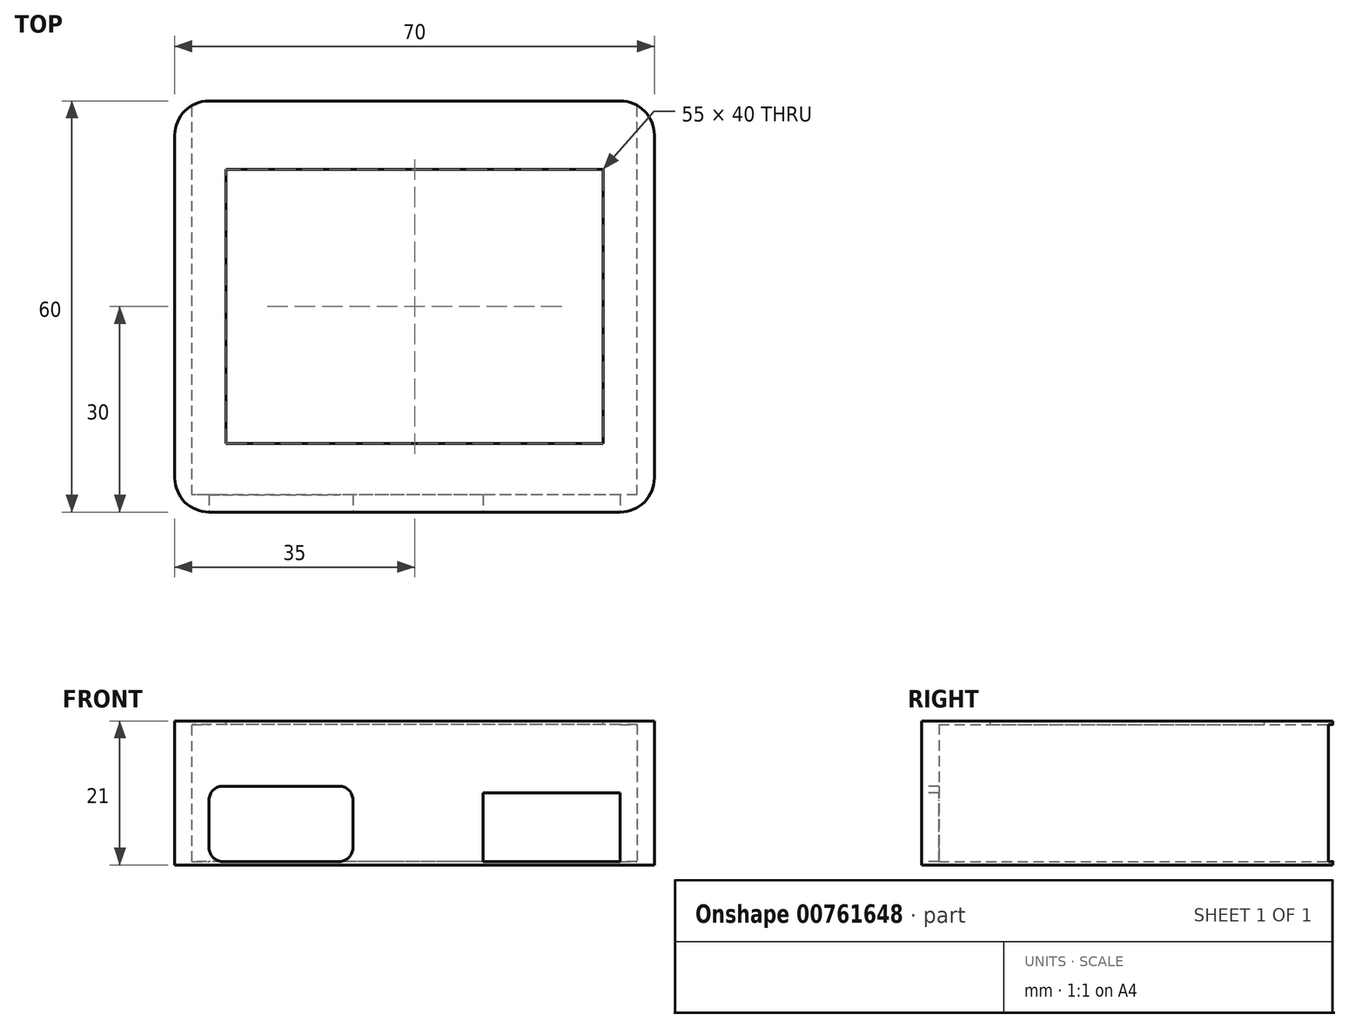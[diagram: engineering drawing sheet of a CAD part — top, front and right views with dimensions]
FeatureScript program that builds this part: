
annotation { "Feature Type Name" : "Feature", "Feature Type Description" : "" }
export const myFeature = defineFeature(function(context is Context, id is Id, definition is map)
    precondition{}
    {
        {
            var Q0;
            Q0=qCreatedBy(makeId("Top.planeOp"),FACE);
            var sketch = newSketch(context, id + "F0", { "sketchPlane" : qUnion([Q0])});
            skLineSegment(sketch, "E0.bottom", {"start": v(-35, 30) * mm, "end": v(35, 30) * mm});
            skLineSegment(sketch, "E0.top", {"start": v(-35, -30) * mm, "end": v(35, -30) * mm});
            skLineSegment(sketch, "E0.left", {"start": v(-35, 30) * mm, "end": v(-35, -30) * mm});
            skLineSegment(sketch, "E0.right", {"start": v(35, 30) * mm, "end": v(35, -30) * mm});
            skSolve(sketch);
        }
        {
            var Q0;
            Q0=makeQuery(id+"F0.imprint","IMPRINT",FACE,{"disambiguationData":[TD([[makeQuery(id+"F0.imprint","IMPRINT",EDGE,{"derivedFrom":sQuery(id+"F0.wireOp",EDGE,"E0.bottom")}),-1.0]])]});
            extrude(context, id + "F1", {"entities" : qUnion([Q0]), "depth" : 21 * mm, "offsetDistance" : 25 * mm});
        }
        {
            var Q0;
            Q0=makeQuery(id+"F1.opExtrude","SWEPT_EDGE",EDGE,{"disambiguationData":[OSD([sQuery(id+"F0.wireOp",EDGE,"E0.top"),sQuery(id+"F0.wireOp",EDGE,"E0.left")])]});
            var Q1;
            Q1=makeQuery(id+"F1.opExtrude","SWEPT_EDGE",EDGE,{"disambiguationData":[OSD([sQuery(id+"F0.wireOp",EDGE,"E0.bottom"),sQuery(id+"F0.wireOp",EDGE,"E0.left")])]});
            var Q2;
            Q2=makeQuery(id+"F1.opExtrude","SWEPT_EDGE",EDGE,{"disambiguationData":[OSD([sQuery(id+"F0.wireOp",EDGE,"E0.bottom"),sQuery(id+"F0.wireOp",EDGE,"E0.right")])]});
            var Q3;
            Q3=makeQuery(id+"F1.opExtrude","SWEPT_EDGE",EDGE,{"disambiguationData":[OSD([sQuery(id+"F0.wireOp",EDGE,"E0.top"),sQuery(id+"F0.wireOp",EDGE,"E0.right")])]});
            fillet(context, id + "F2", {"entities" : qUnion([Q0, Q1, Q2, Q3]), "radius" : 5 * mm, "tangentPropagation" : true, "allowEdgeOverflow" : false});
        }
        {
            var Q0;
            Q0=makeQuery(id+"F1.opExtrude","SWEPT_FACE",FACE,{"disambiguationData":[OSD([sQuery(id+"F0.wireOp",EDGE,"E0.bottom")])]});
            var sketch = newSketch(context, id + "F3", { "sketchPlane" : qUnion([Q0])});
            skLineSegment(sketch, "E1.bottom", {"start": v(-32.5, 20.5) * mm, "end": v(32.5, 20.5) * mm});
            skLineSegment(sketch, "E1.top", {"start": v(-32.5, 0.5) * mm, "end": v(32.5, 0.5) * mm});
            skLineSegment(sketch, "E1.left", {"start": v(-32.5, 20.5) * mm, "end": v(-32.5, 0.5) * mm});
            skLineSegment(sketch, "E1.right", {"start": v(32.5, 20.5) * mm, "end": v(32.5, 0.5) * mm});
            skSolve(sketch);
        }
        {
            var Q0;
            Q0 = qSketchRegion(id + "F3", true);
            extrude(context, id + "F4", {"entities" : qUnion([Q0]), "operationType" : NewBodyOperationType.REMOVE, "oppositeDirection" : true, "depth" : 57.5 * mm, "offsetDistance" : 25 * mm});
        }
        {
            var Q0;
            Q0=makeQuery(id+"F1.opExtrude","CAP_FACE",FACE,{"disambiguationData":[OSD([sQuery(id+"F0.wireOp",EDGE,"E0.bottom"),sQuery(id+"F0.wireOp",EDGE,"E0.top"),sQuery(id+"F0.wireOp",EDGE,"E0.left"),sQuery(id+"F0.wireOp",EDGE,"E0.right")])],"isStart":false});
            var sketch = newSketch(context, id + "F5", { "sketchPlane" : qUnion([Q0])});
            skLineSegment(sketch, "E2.bottom", {"start": v(-27.5, 20) * mm, "end": v(27.5, 20) * mm});
            skLineSegment(sketch, "E2.top", {"start": v(-27.5, -20) * mm, "end": v(27.5, -20) * mm});
            skLineSegment(sketch, "E2.left", {"start": v(-27.5, 20) * mm, "end": v(-27.5, -20) * mm});
            skLineSegment(sketch, "E2.right", {"start": v(27.5, 20) * mm, "end": v(27.5, -20) * mm});
            skSolve(sketch);
        }
        {
            var Q0;
            Q0=makeQuery(id+"F5.imprint","IMPRINT",FACE,{"disambiguationData":[TD([[makeQuery(id+"F5.imprint","IMPRINT",EDGE,{"derivedFrom":sQuery(id+"F5.wireOp",EDGE,"E2.bottom")}),-1.0]])]});
            extrude(context, id + "F6", {"entities" : qUnion([Q0]), "operationType" : NewBodyOperationType.REMOVE, "oppositeDirection" : true, "depth" : 1 * mm, "offsetDistance" : 25 * mm});
        }
        {
            var Q0;
            Q0=makeQuery(id+"F1.opExtrude","SWEPT_FACE",FACE,{"disambiguationData":[OSD([sQuery(id+"F0.wireOp",EDGE,"E0.top")])]});
            var sketch = newSketch(context, id + "F7", { "sketchPlane" : qUnion([Q0])});
            skLineSegment(sketch, "E3.bottom", {"start": v(-11, 11.5) * mm, "end": v(-28, 11.5) * mm});
            skLineSegment(sketch, "E3.top", {"start": v(-11, 0.5) * mm, "end": v(-28, 0.5) * mm});
            skLineSegment(sketch, "E3.left", {"start": v(-9, 9.5) * mm, "end": v(-9, 2.5) * mm});
            skLineSegment(sketch, "E3.right", {"start": v(-30, 9.5) * mm, "end": v(-30, 2.5) * mm});
            skPoint(sketch, "E4.visualSharp", {"position": v(-30, 11.5) * mm});
            skArc(sketch, "E4.filletArc", {"start": v(-28, 11.5) * mm, "mid": v(-29.41, 10.91) * mm, "end": v(-30, 9.5) * mm});
            skPoint(sketch, "E5.visualSharp", {"position": v(-9, 11.5) * mm});
            skArc(sketch, "E5.filletArc", {"start": v(-9, 9.5) * mm, "mid": v(-9.59, 10.91) * mm, "end": v(-11, 11.5) * mm});
            skPoint(sketch, "E6.visualSharp", {"position": v(-9, 0.5) * mm});
            skArc(sketch, "E6.filletArc", {"start": v(-11, 0.5) * mm, "mid": v(-9.59, 1.09) * mm, "end": v(-9, 2.5) * mm});
            skPoint(sketch, "E7.visualSharp", {"position": v(-30, 0.5) * mm});
            skArc(sketch, "E7.filletArc", {"start": v(-30, 2.5) * mm, "mid": v(-29.41, 1.09) * mm, "end": v(-28, 0.5) * mm});
            skSolve(sketch);
        }
        {
            var Q0;
            Q0=makeQuery(id+"F7.imprint","IMPRINT",FACE,{"disambiguationData":[TD([[makeQuery(id+"F7.imprint","IMPRINT",EDGE,{"derivedFrom":sQuery(id+"F7.wireOp",EDGE,"E3.bottom")}),1.0]])]});
            extrude(context, id + "F8", {"entities" : qUnion([Q0]), "operationType" : NewBodyOperationType.REMOVE, "oppositeDirection" : true, "depth" : 5 * mm, "offsetDistance" : 25 * mm});
        }
        {
            var Q0;
            Q0=makeQuery(id+"F1.opExtrude","SWEPT_FACE",FACE,{"disambiguationData":[OSD([sQuery(id+"F0.wireOp",EDGE,"E0.top")])]});
            var sketch = newSketch(context, id + "F9", { "sketchPlane" : qUnion([Q0])});
            skLineSegment(sketch, "E8.bottom", {"start": v(10, 10.5) * mm, "end": v(30, 10.5) * mm});
            skLineSegment(sketch, "E8.top", {"start": v(10, 0.5) * mm, "end": v(30, 0.5) * mm});
            skLineSegment(sketch, "E8.left", {"start": v(10, 10.5) * mm, "end": v(10, 0.5) * mm});
            skLineSegment(sketch, "E8.right", {"start": v(30, 10.5) * mm, "end": v(30, 0.5) * mm});
            skSolve(sketch);
        }
        {
            var Q0;
            Q0=makeQuery(id+"F9.imprint","IMPRINT",FACE,{"disambiguationData":[TD([[makeQuery(id+"F9.imprint","IMPRINT",EDGE,{"derivedFrom":sQuery(id+"F9.wireOp",EDGE,"E8.bottom")}),-1.0]])]});
            extrude(context, id + "F10", {"entities" : qUnion([Q0]), "operationType" : NewBodyOperationType.REMOVE, "oppositeDirection" : true, "depth" : 4 * mm, "offsetDistance" : 25 * mm});
        }
    });
